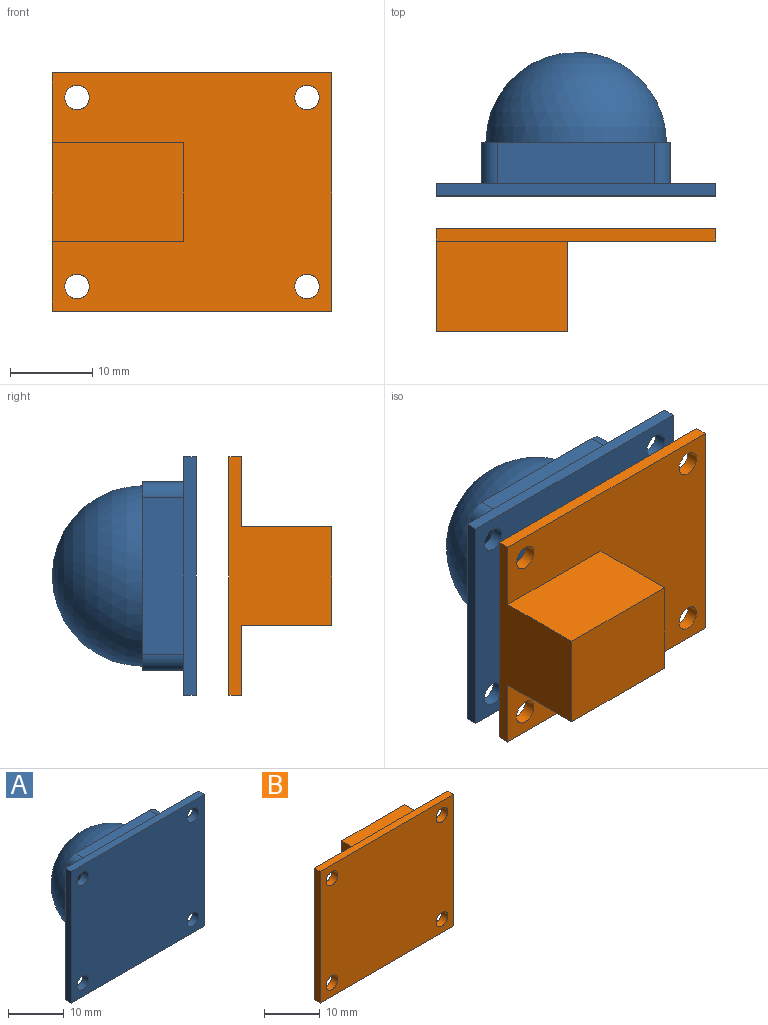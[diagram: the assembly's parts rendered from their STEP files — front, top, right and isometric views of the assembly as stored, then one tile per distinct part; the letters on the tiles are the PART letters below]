
ASSEMBLY  parts=2 mates=1
PART A: 20 faces, bbox 34x17.5x29 mm
  f0: plane 19x5mm, normal (0,0,-1), area 95mm2, adj f1,f7,f8,f19
  f1: cylinder r=2mm len=5mm, axis (0,1,0), area 15.7mm2, adj f0,f2,f8,f19
  f2: plane 19x5mm, normal (1,0,0), area 95mm2, adj f1,f3,f8,f19
  f3: cylinder r=2mm len=5mm, axis (0,1,0), area 15.7mm2, adj f2,f4,f8,f19
  f4: plane 19x5mm, normal (0,0,1), area 95mm2, adj f3,f5,f8,f19
  f5: cylinder r=2mm len=5mm, axis (0,1,0), area 15.7mm2, adj f4,f6,f8,f19
  f6: plane 19x5mm, normal (-1,0,0), area 95mm2, adj f5,f7,f8,f19
  f7: cylinder r=2mm len=5mm, axis (0,1,0), area 15.7mm2, adj f0,f6,f8,f19
  f8: plane 23x23mm, normal (0,1,0), area 145.4mm2, adj f0,f1,f2,f3,f4,f5,f6,f7
  f9: sphere r=11mm, area 760.3mm2, adj f8
  f10: plane 34x1.5mm, normal (0,0,1), area 51mm2, adj f11,f17,f18,f19
  f11: plane 29x1.5mm, normal (-1,0,0), area 43.5mm2, adj f10,f12,f18,f19
  f12: plane 34x1.5mm, normal (0,0,-1), area 51mm2, adj f11,f17,f18,f19
  f13: cylinder r=1.5mm len=3mm, axis (0,1,0), area 14.1mm2, adj f18,f19
  f14: cylinder r=1.5mm len=3mm, axis (0,1,0), area 14.1mm2, adj f18,f19
  f15: cylinder r=1.5mm len=3mm, axis (0,1,0), area 14.1mm2, adj f18,f19
  f16: cylinder r=1.5mm len=3mm, axis (0,1,0), area 14.1mm2, adj f18,f19
  f17: plane 29x1.5mm, normal (1,0,0), area 43.5mm2, adj f10,f12,f18,f19
  f18: plane 34x29mm, normal (0,-1,0), area 957.7mm2, adj f10,f11,f12,f13,f14,f15,f16,f17
  f19: plane 34x29mm, normal (0,1,0), area 432.2mm2, adj f0,f1,f2,f3,f4,f5,f6,f7
PART B: 14 faces, bbox 34x12.5x29 mm
  f0: plane 29x12.5mm, normal (1,0,0), area 175.5mm2, adj f1,f6,f8,f9,f10,f12,f13
  f1: plane 34x1.5mm, normal (0,0,1), area 51mm2, adj f0,f2,f8,f9
  f2: plane 29x1.5mm, normal (-1,0,0), area 43.5mm2, adj f1,f6,f8,f9
  f3: cylinder r=1.5mm len=3mm, axis (0,1,0), area 14.1mm2, adj f8,f9
  f4: cylinder r=1.5mm len=3mm, axis (0,1,0), area 14.1mm2, adj f8,f9
  f5: cylinder r=1.5mm len=3mm, axis (0,1,0), area 14.1mm2, adj f8,f9
  f6: plane 34x1.5mm, normal (0,0,-1), area 51mm2, adj f0,f2,f8,f9
  f7: cylinder r=1.5mm len=3mm, axis (0,1,0), area 14.1mm2, adj f8,f9
  f8: plane 34x29mm, normal (0,-1,0), area 957.7mm2, adj f0,f1,f2,f3,f4,f5,f6,f7
  f9: plane 34x29mm, normal (0,1,0), area 765.7mm2, adj f0,f1,f2,f3,f4,f5,f6,f7
  f10: plane 16x11mm, normal (0,0,1), area 176mm2, adj f0,f9,f11,f13
  f11: plane 12x11mm, normal (-1,0,0), area 132mm2, adj f9,f10,f12,f13
  f12: plane 16x11mm, normal (0,0,-1), area 176mm2, adj f0,f9,f11,f13
  f13: plane 16x12mm, normal (0,1,0), area 192mm2, adj f0,f10,f11,f12
PLACE A t=(8.45,-3.46,8.31)mm
PLACE B rot(axis=(0,0,1),180deg) t=(-27.54,-15.46,12.02)mm
MATE fastened B.f5 <-> A.f15  axis (0,1,0) through (22.45,-13.96,19.81)mm
